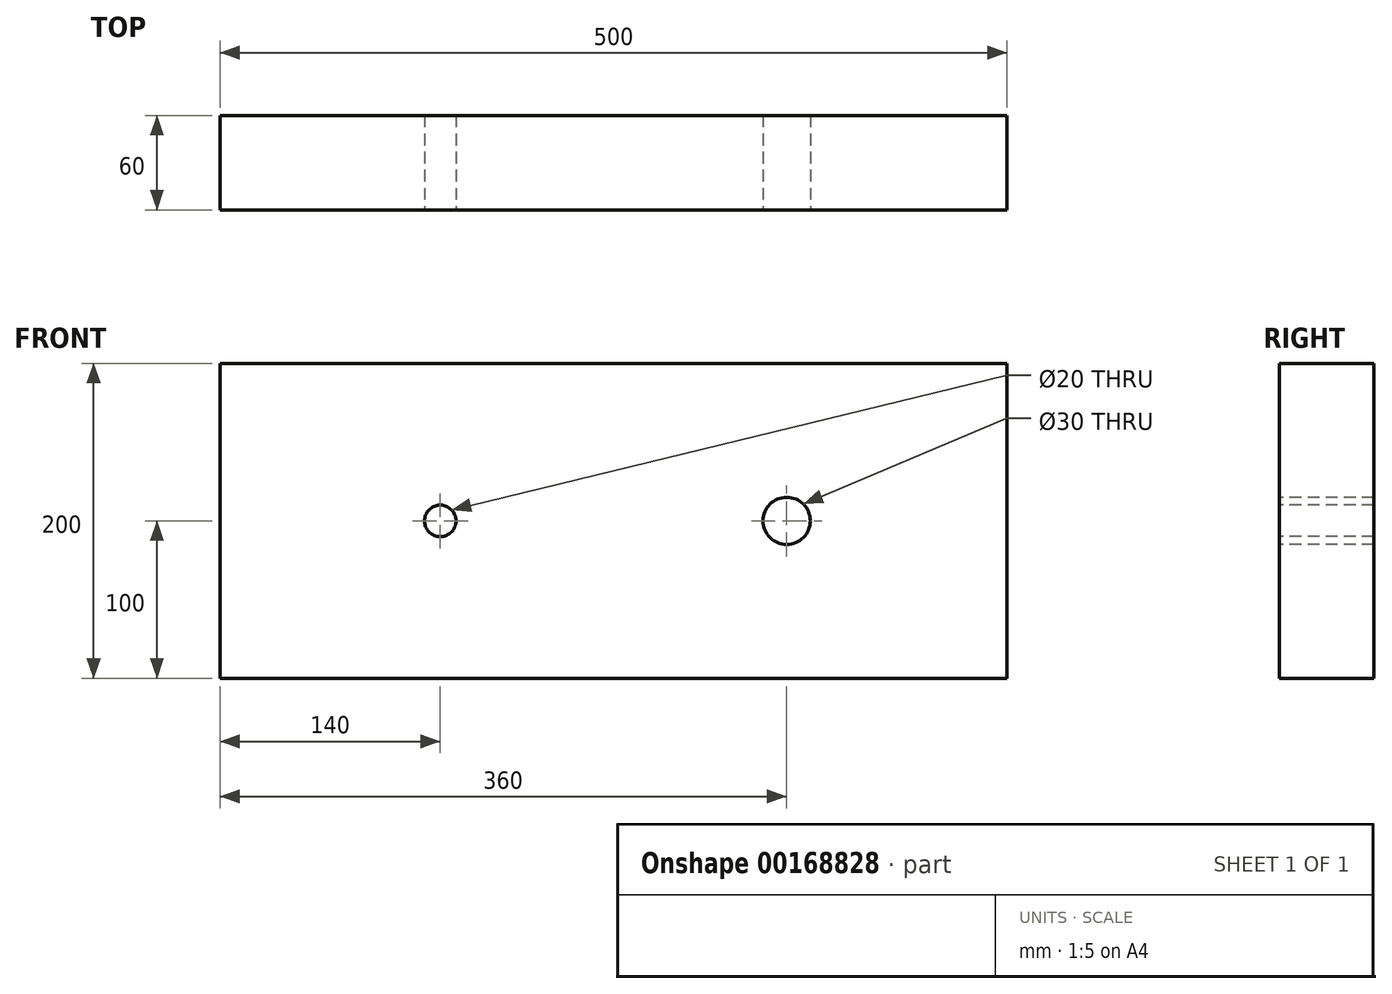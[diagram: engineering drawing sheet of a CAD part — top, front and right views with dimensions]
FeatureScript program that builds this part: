
annotation { "Feature Type Name" : "Feature", "Feature Type Description" : "" }
export const myFeature = defineFeature(function(context is Context, id is Id, definition is map)
    precondition{}
    {
        {
            assignVariable(context, id + "F0", {"name" : "t", "anyValue" : 60 * mm});
        }
        {
            var Q0;
            Q0=qCreatedBy(makeId("Front.planeOp"),FACE);
            var sketch = newSketch(context, id + "F1", { "sketchPlane" : qUnion([Q0])});
            skLineSegment(sketch, "E0.bottom", {"start": v(250, -100) * mm, "end": v(-250, -100) * mm});
            skLineSegment(sketch, "E0.top", {"start": v(250, 100) * mm, "end": v(-250, 100) * mm});
            skLineSegment(sketch, "E0.left", {"start": v(250, -100) * mm, "end": v(250, 100) * mm});
            skLineSegment(sketch, "E0.right", {"start": v(-250, -100) * mm, "end": v(-250, 100) * mm});
            skPoint(sketch, "E0.middle", {"position": v(0, 0) * mm});
            skSolve(sketch);
        }
        {
            var Q0;
            Q0=qSketchRegion(id+"F1",true);
            extrude(context, id + "F2", {"entities" : qUnion([Q0]), "depth" : getVariable(context, 't')});
        }
        {
            var Q0;
            Q0=makeQuery(id+"F2.opExtrude","CAP_FACE",FACE,{"disambiguationData":[OSD([sQuery(id+"F1.wireOp",EDGE,"E0.bottom"),sQuery(id+"F1.wireOp",EDGE,"E0.top"),sQuery(id+"F1.wireOp",EDGE,"E0.left"),sQuery(id+"F1.wireOp",EDGE,"E0.right")])],"isStart":false});
            var sketch = newSketch(context, id + "F3", { "sketchPlane" : qUnion([Q0])});
            skCircle(sketch, "E1", {"center": v(110, 0) * mm, "radius": 15 * mm});
            skLineSegment(sketch, "E2", {"start": v(110, 100) * mm, "end": v(110, 0) * mm, "construction": true});
            skLineSegment(sketch, "E3", {"start": v(250, 0) * mm, "end": v(110, 0) * mm, "construction": true});
            skCircle(sketch, "E4", {"center": v(-110, 0) * mm, "radius": 10 * mm});
            skLineSegment(sketch, "E5", {"start": v(-110, 0) * mm, "end": v(-110, 100) * mm, "construction": true});
            skLineSegment(sketch, "E6", {"start": v(-110, 0) * mm, "end": v(-250, 0) * mm, "construction": true});
            skSolve(sketch);
        }
        {
            var Q0;
            Q0=qSketchRegion(id+"F3",true);
            extrude(context, id + "F4", {"entities" : qUnion([Q0]), "operationType" : NewBodyOperationType.REMOVE, "endBound" : BoundingType.THROUGH_ALL, "oppositeDirection" : true, "depth" : 25 * mm});
        }
    });
